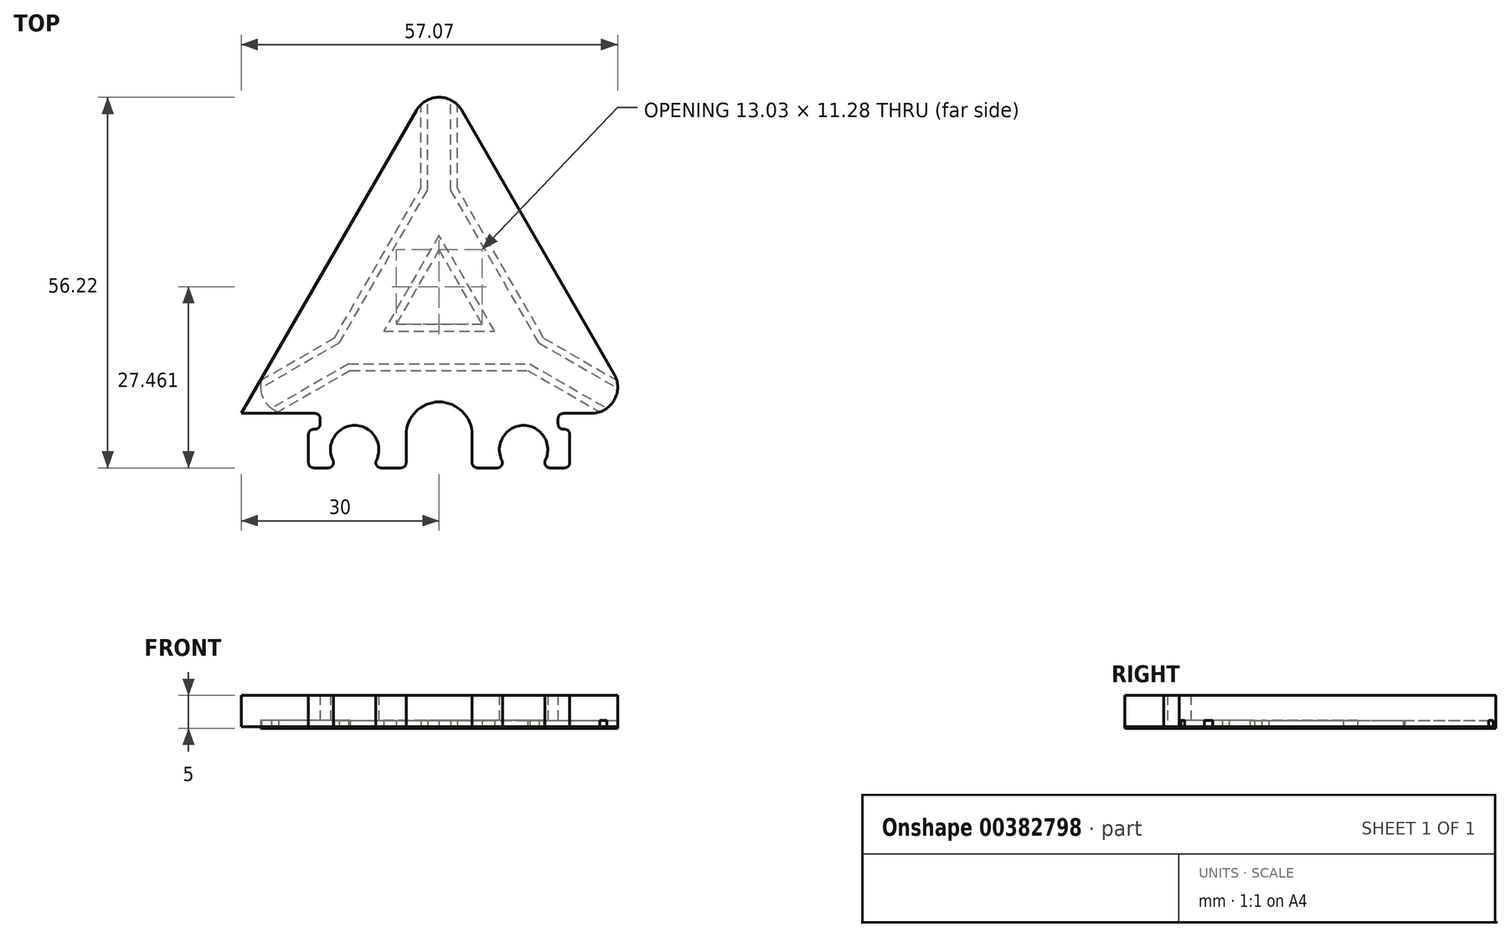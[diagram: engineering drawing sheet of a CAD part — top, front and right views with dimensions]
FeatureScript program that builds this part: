
annotation { "Feature Type Name" : "Feature", "Feature Type Description" : "" }
export const myFeature = defineFeature(function(context is Context, id is Id, definition is map)
    precondition{}
    {
        {
            var Q0;
            Q0=qCreatedBy(makeId("Top.planeOp"),FACE);
            var sketch = newSketch(context, id + "F0", { "sketchPlane" : qUnion([Q0])});
            skArc(sketch, "E0", {"start": v(0, 5) * mm, "mid": v(-3.54, 3.54) * mm, "end": v(-5, 0) * mm});
            skLineSegment(sketch, "E1", {"start": v(-5, 0) * mm, "end": v(-5, -5) * mm});
            skPoint(sketch, "E2.start.orphan", {"position": v(0, 5) * mm});
            skPoint(sketch, "E3.start.orphan", {"position": v(0, -5) * mm});
            skLineSegment(sketch, "E4", {"start": v(-5, -5) * mm, "end": v(-10.4, -5) * mm});
            skArc(sketch, "E5", {"start": v(-10.4, -5) * mm, "mid": v(-12.8, 1.43) * mm, "end": v(-15.22, -5) * mm});
            skPoint(sketch, "E6.end.orphan", {"position": v(-15.22, -5) * mm});
            skPoint(sketch, "E7.start.orphan", {"position": v(-12.8, -5) * mm});
            skLineSegment(sketch, "E8", {"start": v(-15.22, -5) * mm, "end": v(-19.82, -5) * mm});
            skLineSegment(sketch, "E9", {"start": v(-19.82, -5) * mm, "end": v(-19.82, 0.86) * mm});
            skLineSegment(sketch, "E10", {"start": v(-19.82, 0.86) * mm, "end": v(-18.04, 0.86) * mm});
            skLineSegment(sketch, "E11", {"start": v(-18.04, 0.86) * mm, "end": v(-18.04, 3.26) * mm});
            skLineSegment(sketch, "E12", {"start": v(0, -5) * mm, "end": v(0, -3.9) * mm});
            skLineSegment(sketch, "E13", {"start": v(0, 10.27) * mm, "end": v(0, -5) * mm, "construction": true});
            skArc(sketch, "E14.MirrorCS", {"start": v(0, 5) * mm, "mid": v(3.54, 3.54) * mm, "end": v(5, 0) * mm});
            skLineSegment(sketch, "E15.MirrorCS", {"start": v(5, 0) * mm, "end": v(5, -5) * mm});
            skLineSegment(sketch, "E16.MirrorCS", {"start": v(5, -5) * mm, "end": v(10.4, -5) * mm});
            skArc(sketch, "E17.MirrorCS", {"start": v(10.4, -5) * mm, "mid": v(12.8, 1.43) * mm, "end": v(15.22, -5) * mm});
            skLineSegment(sketch, "E18.MirrorCS", {"start": v(15.22, -5) * mm, "end": v(19.82, -5) * mm});
            skLineSegment(sketch, "E19.MirrorCS", {"start": v(19.82, -5) * mm, "end": v(19.82, 0.86) * mm});
            skLineSegment(sketch, "E20.MirrorCS", {"start": v(19.82, 0.86) * mm, "end": v(18.04, 0.86) * mm});
            skLineSegment(sketch, "E21.MirrorCS", {"start": v(18.04, 0.86) * mm, "end": v(18.04, 3.26) * mm});
            skLineSegment(sketch, "E22", {"start": v(-18.04, 3.26) * mm, "end": v(-30, 3.26) * mm});
            skLineSegment(sketch, "E23.bottom", {"start": v(-30, 3.26) * mm, "end": v(-18.04, 3.26) * mm});
            skLineSegment(sketch, "E24.trimOffspring", {"start": v(18.04, 3.26) * mm, "end": v(30, 3.26) * mm});
            skLineSegment(sketch, "E25", {"start": v(-30, 3.26) * mm, "end": v(0, 55.22) * mm});
            skLineSegment(sketch, "E26", {"start": v(30, 3.26) * mm, "end": v(0, 55.22) * mm});
            skSolve(sketch);
        }
        {
            var Q0;
            Q0=makeQuery(id+"F0.imprint","IMPRINT",FACE,{"disambiguationData":[TD([[makeQuery(id+"F0.imprint","IMPRINT",EDGE,{"derivedFrom":sQuery(id+"F0.wireOp",EDGE,"E0")}),-1.0]])]});
            extrude(context, id + "F1", {"entities" : qUnion([Q0]), "depth" : 4.8 * mm});
        }
        {
            var Q0;
            Q0=makeQuery(id+"F1.opExtrude","SWEPT_EDGE",EDGE,{"disambiguationData":[OSD([sQuery(id+"F0.wireOp",EDGE,"E24.trimOffspring"),sQuery(id+"F0.wireOp",EDGE,"E26")])]});
            var Q1;
            Q1=makeQuery(id+"F1.opExtrude","SWEPT_EDGE",EDGE,{"disambiguationData":[OSD([sQuery(id+"F0.wireOp",EDGE,"E25"),sQuery(id+"F0.wireOp",EDGE,"E26")])]});
            var Q2;
            Q2=makeQuery(id+"F1.opExtrude","SWEPT_EDGE",EDGE,{"disambiguationData":[OSD([sQuery(id+"F0.wireOp",EDGE,"E23.bottom"),sQuery(id+"F0.wireOp",EDGE,"E25")])]});
            fillet(context, id + "F2", {"entities" : qUnion([Q0, Q1, Q2]), "radius" : 4 * mm, "tangentPropagation" : true, "allowEdgeOverflow" : false});
        }
        {
            var Q0;
            Q0=makeQuery(id+"F1.opExtrude","CAP_FACE",FACE,{"disambiguationData":[OSD([sQuery(id+"F0.wireOp",EDGE,"E0"),sQuery(id+"F0.wireOp",EDGE,"E1"),sQuery(id+"F0.wireOp",EDGE,"E4"),sQuery(id+"F0.wireOp",EDGE,"E5"),sQuery(id+"F0.wireOp",EDGE,"E8"),sQuery(id+"F0.wireOp",EDGE,"E9"),sQuery(id+"F0.wireOp",EDGE,"E10"),sQuery(id+"F0.wireOp",EDGE,"E11"),sQuery(id+"F0.wireOp",EDGE,"E14.MirrorCS"),sQuery(id+"F0.wireOp",EDGE,"E15.MirrorCS"),sQuery(id+"F0.wireOp",EDGE,"E16.MirrorCS"),sQuery(id+"F0.wireOp",EDGE,"E17.MirrorCS"),sQuery(id+"F0.wireOp",EDGE,"E18.MirrorCS"),sQuery(id+"F0.wireOp",EDGE,"E19.MirrorCS"),sQuery(id+"F0.wireOp",EDGE,"E20.MirrorCS"),sQuery(id+"F0.wireOp",EDGE,"E21.MirrorCS"),sQuery(id+"F0.wireOp",EDGE,"E23.bottom"),sQuery(id+"F0.wireOp",EDGE,"E24.trimOffspring"),sQuery(id+"F0.wireOp",EDGE,"E25"),sQuery(id+"F0.wireOp",EDGE,"E26")])],"isStart":true});
            var sketch = newSketch(context, id + "F3", { "sketchPlane" : qUnion([Q0])});
            skPoint(sketch, "E27.orphan", {"position": v(15, -29.24) * mm});
            skPoint(sketch, "E28", {"position": v(0, -20.58) * mm});
            skPoint(sketch, "E29.start.orphan", {"position": v(0, -51.22) * mm});
            skPoint(sketch, "E30.end.orphan", {"position": v(-26.54, -5.26) * mm});
            skArc(sketch, "E31.cCircle", {"start": v(-8.49, -25.48) * mm, "mid": v(8.49, -25.48) * mm, "end": v(0, -10.78) * mm, "construction": true});
            skLineSegment(sketch, "E31.0", {"start": v(0, -10.78) * mm, "end": v(13.74, -10.78) * mm});
            skLineSegment(sketch, "E31.1", {"start": v(15.15, -13.95) * mm, "end": v(1.74, -37.18) * mm});
            skPoint(sketch, "E31.0.midPoint", {"position": v(0, -10.78) * mm});
            skLineSegment(sketch, "E32.MirrorCS", {"start": v(13.74, -10.78) * mm, "end": v(0, -10.78) * mm});
            skPoint(sketch, "E33.start.orphan", {"position": v(8.49, -25.48) * mm});
            skPoint(sketch, "E34.orphan", {"position": v(-16.98, -10.78) * mm});
            skLineSegment(sketch, "E35", {"start": v(15.15, -13.95) * mm, "end": v(27.07, -7.07) * mm});
            skLineSegment(sketch, "E36", {"start": v(13.74, -10.78) * mm, "end": v(25.43, -4.03) * mm});
            skPoint(sketch, "E37.orphan", {"position": v(16.98, -10.78) * mm});
            skLineSegment(sketch, "E38.MirrorCS", {"start": v(1.74, -37.18) * mm, "end": v(1.74, -50.82) * mm});
            skPoint(sketch, "E39.orphan", {"position": v(0, -40.19) * mm});
            skCircle(sketch, "E40.cCircle", {"center": v(0, -20.58) * mm, "radius": 3.76 * mm, "construction": true});
            skPoint(sketch, "E40.0.midPoint", {"position": v(0, -16.82) * mm});
            skPoint(sketch, "E41.orphan", {"position": v(0, -28.1) * mm});
            skPoint(sketch, "E42.orphan", {"position": v(-6.51, -16.82) * mm});
            skPoint(sketch, "E40.1.start.orphan", {"position": v(6.51, -16.82) * mm});
            skLineSegment(sketch, "E43.0", {"start": v(2.74, -37.45) * mm, "end": v(2.74, -50.14) * mm});
            skLineSegment(sketch, "E43.1", {"start": v(15.88, -14.68) * mm, "end": v(2.74, -37.45) * mm});
            skLineSegment(sketch, "E43.2", {"start": v(15.88, -14.68) * mm, "end": v(26.93, -8.3) * mm});
            skLineSegment(sketch, "E44.1", {"start": v(13.47, -9.78) * mm, "end": v(0, -9.78) * mm});
            skLineSegment(sketch, "E44.2", {"start": v(13.47, -9.78) * mm, "end": v(24.38, -3.48) * mm});
            skLineSegment(sketch, "E45.0", {"start": v(-6.51, -16.82) * mm, "end": v(6.51, -16.82) * mm});
            skLineSegment(sketch, "E45.1", {"start": v(6.51, -16.82) * mm, "end": v(0, -28.1) * mm});
            skLineSegment(sketch, "E45.2", {"start": v(0, -28.1) * mm, "end": v(-6.51, -16.82) * mm});
            skCircle(sketch, "E46.cCircle", {"center": v(0, -20.58) * mm, "radius": 4.86 * mm, "construction": true});
            skLineSegment(sketch, "E46.0", {"start": v(-8.42, -15.72) * mm, "end": v(8.42, -15.72) * mm});
            skLineSegment(sketch, "E46.1", {"start": v(8.42, -15.72) * mm, "end": v(0, -30.3) * mm});
            skLineSegment(sketch, "E46.2", {"start": v(0, -30.3) * mm, "end": v(-8.42, -15.72) * mm});
            skPoint(sketch, "E46.0.midPoint", {"position": v(0, -15.72) * mm});
            skArc(sketch, "E47.0", {"start": v(26.93, -8.3) * mm, "mid": v(27.05, -7.7) * mm, "end": v(27.07, -7.07) * mm});
            skPoint(sketch, "E48.orphan", {"position": v(-26.54, -9.26) * mm});
            skPoint(sketch, "E49.orphan", {"position": v(-23.07, -3.26) * mm});
            skArc(sketch, "E50.trimOffspring", {"start": v(-26.54, -5.26) * mm, "mid": v(-27.02, -6.63) * mm, "end": v(-26.99, -8.08) * mm});
            skPoint(sketch, "E51.orphan", {"position": v(26.76, -3.26) * mm});
            skArc(sketch, "E52.trimOffspring", {"start": v(25.43, -4.03) * mm, "mid": v(24.92, -3.71) * mm, "end": v(24.38, -3.48) * mm});
            skPoint(sketch, "E53.orphan", {"position": v(26.54, -9.26) * mm});
            skPoint(sketch, "E54.orphan", {"position": v(23.07, -3.26) * mm});
            skArc(sketch, "E55.trimOffspring", {"start": v(0, -51.22) * mm, "mid": v(2, -50.69) * mm, "end": v(3.46, -49.22) * mm});
            skLineSegment(sketch, "E56", {"start": v(0, -5) * mm, "end": v(0, -56.8) * mm});
            skPoint(sketch, "E57.0.start.orphan", {"position": v(-3.46, -49.22) * mm});
            skLineSegment(sketch, "E58.MirrorCS", {"start": v(-15.15, -13.95) * mm, "end": v(-1.74, -37.18) * mm});
            skLineSegment(sketch, "E59.MirrorCS", {"start": v(-15.88, -14.68) * mm, "end": v(-2.74, -37.45) * mm});
            skLineSegment(sketch, "E60.MirrorCS", {"start": v(-2.74, -37.45) * mm, "end": v(-2.74, -50.14) * mm});
            skLineSegment(sketch, "E61.MirrorCS", {"start": v(-1.74, -37.18) * mm, "end": v(-1.74, -50.82) * mm});
            skLineSegment(sketch, "E62.MirrorCS", {"start": v(-15.88, -14.68) * mm, "end": v(-26.93, -8.3) * mm});
            skLineSegment(sketch, "E63.MirrorCS", {"start": v(-15.15, -13.95) * mm, "end": v(-27.07, -7.07) * mm});
            skLineSegment(sketch, "E64.MirrorCS", {"start": v(-13.74, -10.78) * mm, "end": v(0, -10.78) * mm});
            skLineSegment(sketch, "E65.MirrorCS", {"start": v(-13.47, -9.78) * mm, "end": v(0, -9.78) * mm});
            skLineSegment(sketch, "E66.MirrorCS", {"start": v(-13.47, -9.78) * mm, "end": v(-24.38, -3.48) * mm});
            skLineSegment(sketch, "E67.MirrorCS", {"start": v(-13.74, -10.78) * mm, "end": v(-25.43, -4.03) * mm});
            skArc(sketch, "E68.0", {"start": v(-2.74, -50.14) * mm, "mid": v(-2.26, -50.52) * mm, "end": v(-1.74, -50.82) * mm});
            skArc(sketch, "E69.0", {"start": v(-24.38, -3.48) * mm, "mid": v(-24.92, -3.71) * mm, "end": v(-25.43, -4.03) * mm});
            skArc(sketch, "E70.trimOffspring", {"start": v(-27.07, -7.07) * mm, "mid": v(-27.05, -7.7) * mm, "end": v(-26.93, -8.3) * mm});
            skArc(sketch, "E71.trimOffspring", {"start": v(1.74, -50.82) * mm, "mid": v(2.26, -50.52) * mm, "end": v(2.74, -50.14) * mm});
            skSolve(sketch);
        }
        {
            var Q0;
            Q0 = qSketchRegion(id + "F3", true);
            extrude(context, id + "F4", {"entities" : qUnion([Q0]), "operationType" : NewBodyOperationType.REMOVE, "oppositeDirection" : true, "depth" : 1 * mm});
        }
        {
            var Q0;
            Q0 = qSketchRegion(id + "F3", true);
            extrude(context, id + "F5", {"entities" : qUnion([Q0]), "oppositeDirection" : true, "depth" : 1 * mm});
        }
        {
            var Q0;
            Q0=makeQuery(id+"F1.opExtrude","SWEPT_EDGE",EDGE,{"disambiguationData":[OSD([sQuery(id+"F0.wireOp",EDGE,"E21.MirrorCS"),sQuery(id+"F0.wireOp",EDGE,"E24.trimOffspring")])]});
            var Q1;
            Q1=makeQuery(id+"F1.opExtrude","SWEPT_EDGE",EDGE,{"disambiguationData":[OSD([sQuery(id+"F0.wireOp",EDGE,"E20.MirrorCS"),sQuery(id+"F0.wireOp",EDGE,"E21.MirrorCS")])]});
            var Q2;
            Q2=makeQuery(id+"F1.opExtrude","SWEPT_EDGE",EDGE,{"disambiguationData":[OSD([sQuery(id+"F0.wireOp",EDGE,"E19.MirrorCS"),sQuery(id+"F0.wireOp",EDGE,"E20.MirrorCS")])]});
            var Q3;
            Q3=makeQuery(id+"F1.opExtrude","SWEPT_EDGE",EDGE,{"disambiguationData":[OSD([sQuery(id+"F0.wireOp",EDGE,"E18.MirrorCS"),sQuery(id+"F0.wireOp",EDGE,"E19.MirrorCS")])]});
            var Q4;
            Q4=makeQuery(id+"F1.opExtrude","SWEPT_EDGE",EDGE,{"disambiguationData":[OSD([sQuery(id+"F0.wireOp",EDGE,"E17.MirrorCS"),sQuery(id+"F0.wireOp",EDGE,"E18.MirrorCS")])]});
            var Q5;
            Q5=makeQuery(id+"F1.opExtrude","SWEPT_EDGE",EDGE,{"disambiguationData":[OSD([sQuery(id+"F0.wireOp",EDGE,"E16.MirrorCS"),sQuery(id+"F0.wireOp",EDGE,"E17.MirrorCS")])]});
            var Q6;
            Q6=makeQuery(id+"F1.opExtrude","SWEPT_EDGE",EDGE,{"disambiguationData":[OSD([sQuery(id+"F0.wireOp",EDGE,"E15.MirrorCS"),sQuery(id+"F0.wireOp",EDGE,"E16.MirrorCS")])]});
            var Q7;
            Q7=makeQuery(id+"F1.opExtrude","SWEPT_EDGE",EDGE,{"disambiguationData":[OSD([sQuery(id+"F0.wireOp",EDGE,"E1"),sQuery(id+"F0.wireOp",EDGE,"E4")])]});
            var Q8;
            Q8=makeQuery(id+"F1.opExtrude","SWEPT_EDGE",EDGE,{"disambiguationData":[OSD([sQuery(id+"F0.wireOp",EDGE,"E4"),sQuery(id+"F0.wireOp",EDGE,"E5")])]});
            var Q9;
            Q9=makeQuery(id+"F1.opExtrude","SWEPT_EDGE",EDGE,{"disambiguationData":[OSD([sQuery(id+"F0.wireOp",EDGE,"E5"),sQuery(id+"F0.wireOp",EDGE,"E8")])]});
            var Q10;
            Q10=makeQuery(id+"F1.opExtrude","SWEPT_EDGE",EDGE,{"disambiguationData":[OSD([sQuery(id+"F0.wireOp",EDGE,"E8"),sQuery(id+"F0.wireOp",EDGE,"E9")])]});
            var Q11;
            Q11=makeQuery(id+"F1.opExtrude","SWEPT_EDGE",EDGE,{"disambiguationData":[OSD([sQuery(id+"F0.wireOp",EDGE,"E9"),sQuery(id+"F0.wireOp",EDGE,"E10")])]});
            var Q12;
            Q12=makeQuery(id+"F1.opExtrude","SWEPT_EDGE",EDGE,{"disambiguationData":[OSD([sQuery(id+"F0.wireOp",EDGE,"E10"),sQuery(id+"F0.wireOp",EDGE,"E11")])]});
            var Q13;
            Q13=makeQuery(id+"F1.opExtrude","SWEPT_EDGE",EDGE,{"disambiguationData":[OSD([sQuery(id+"F0.wireOp",EDGE,"E11"),sQuery(id+"F0.wireOp",EDGE,"E23.bottom")])]});
            fillet(context, id + "F6", {"entities" : qUnion([Q0, Q1, Q2, Q3, Q4, Q5, Q6, Q7, Q8, Q9, Q10, Q11, Q12, Q13]), "radius" : .8 * mm, "tangentPropagation" : true, "allowEdgeOverflow" : false});
        }
        {
            var Q0;
            {var subQ0=sQuery(id+"F0.wireOp",EDGE,"E26");var subQ1=sQuery(id+"F0.wireOp",EDGE,"E25");var subQ2=sQuery(id+"F0.wireOp",EDGE,"E24.trimOffspring");Q0=makeQuery(id+"F4.boolean.opBoolean","SPLIT",FACE,{"disambiguationData":[TD([makeQuery(id+"F1.opExtrude","SWEPT_FACE",FACE,{"disambiguationData":[OSD([subQ0])]})])],"derivedFrom":makeQuery(id+"F1.opExtrude","CAP_FACE",FACE,{"disambiguationData":[OSD([sQuery(id+"F0.wireOp",EDGE,"E0"),sQuery(id+"F0.wireOp",EDGE,"E1"),sQuery(id+"F0.wireOp",EDGE,"E4"),sQuery(id+"F0.wireOp",EDGE,"E5"),sQuery(id+"F0.wireOp",EDGE,"E8"),sQuery(id+"F0.wireOp",EDGE,"E9"),sQuery(id+"F0.wireOp",EDGE,"E10"),sQuery(id+"F0.wireOp",EDGE,"E11"),sQuery(id+"F0.wireOp",EDGE,"E14.MirrorCS"),sQuery(id+"F0.wireOp",EDGE,"E15.MirrorCS"),sQuery(id+"F0.wireOp",EDGE,"E16.MirrorCS"),sQuery(id+"F0.wireOp",EDGE,"E17.MirrorCS"),sQuery(id+"F0.wireOp",EDGE,"E18.MirrorCS"),sQuery(id+"F0.wireOp",EDGE,"E19.MirrorCS"),sQuery(id+"F0.wireOp",EDGE,"E20.MirrorCS"),sQuery(id+"F0.wireOp",EDGE,"E21.MirrorCS"),sQuery(id+"F0.wireOp",EDGE,"E23.bottom"),subQ2,subQ1,subQ0])],"isStart":true})});}
            var sketch = newSketch(context, id + "F7", { "sketchPlane" : qUnion([Q0])});
            skLineSegment(sketch, "E72.0", {"start": v(26.54, -9.26) * mm, "end": v(3.46, -49.22) * mm});
            skArc(sketch, "E73.0", {"start": v(2.74, -50.14) * mm, "mid": v(3.13, -49.7) * mm, "end": v(3.46, -49.22) * mm});
            skPoint(sketch, "E74.0", {"position": v(2.26, -50.52) * mm});
            skArc(sketch, "E75.0", {"start": v(1.74, -50.82) * mm, "mid": v(2.26, -50.52) * mm, "end": v(2.74, -50.14) * mm});
            skArc(sketch, "E76.0", {"start": v(-1.74, -50.82) * mm, "mid": v(0, -51.22) * mm, "end": v(1.74, -50.82) * mm});
            skArc(sketch, "E77.0", {"start": v(-2.74, -50.14) * mm, "mid": v(-2.26, -50.52) * mm, "end": v(-1.74, -50.82) * mm});
            skArc(sketch, "E78.0", {"start": v(-3.46, -49.22) * mm, "mid": v(-3.13, -49.7) * mm, "end": v(-2.74, -50.14) * mm});
            skLineSegment(sketch, "E79.0", {"start": v(-26.54, -9.26) * mm, "end": v(-3.46, -49.22) * mm});
            skArc(sketch, "E80.0", {"start": v(-26.93, -8.3) * mm, "mid": v(-26.77, -8.8) * mm, "end": v(-26.54, -9.26) * mm});
            skArc(sketch, "E80.1", {"start": v(-27.07, -7.07) * mm, "mid": v(-27.05, -7.7) * mm, "end": v(-26.93, -8.3) * mm});
            skArc(sketch, "E80.2", {"start": v(-25.43, -4.03) * mm, "mid": v(-26.6, -5.36) * mm, "end": v(-27.07, -7.07) * mm});
            skArc(sketch, "E81.0", {"start": v(-24.38, -3.48) * mm, "mid": v(-24.92, -3.71) * mm, "end": v(-25.43, -4.03) * mm});
            skArc(sketch, "E82.0", {"start": v(-23.07, -3.26) * mm, "mid": v(-23.73, -3.32) * mm, "end": v(-24.38, -3.48) * mm});
            skLineSegment(sketch, "E83.0", {"start": v(-23.07, -3.26) * mm, "end": v(-18.84, -3.26) * mm});
            skArc(sketch, "E84.0", {"start": v(-18.04, -2.46) * mm, "mid": v(-18.27, -3.03) * mm, "end": v(-18.84, -3.26) * mm});
            skLineSegment(sketch, "E85.0", {"start": v(-18.04, -1.66) * mm, "end": v(-18.04, -2.46) * mm});
            skArc(sketch, "E86.0", {"start": v(-18.84, -0.86) * mm, "mid": v(-18.27, -1.1) * mm, "end": v(-18.04, -1.66) * mm});
            skArc(sketch, "E87.0", {"start": v(-19.82, -0.06) * mm, "mid": v(-19.58, -0.63) * mm, "end": v(-19.02, -0.86) * mm});
            skPoint(sketch, "E88.0", {"position": v(-18.93, -0.86) * mm});
            skLineSegment(sketch, "E89.0", {"start": v(-19.02, -0.86) * mm, "end": v(-18.84, -0.86) * mm});
            skLineSegment(sketch, "E90.0", {"start": v(-19.82, 4.2) * mm, "end": v(-19.82, -0.06) * mm});
            skArc(sketch, "E91.0", {"start": v(-19.02, 5) * mm, "mid": v(-19.58, 4.77) * mm, "end": v(-19.82, 4.2) * mm});
            skLineSegment(sketch, "E92.0", {"start": v(-16.82, 5) * mm, "end": v(-19.02, 5) * mm});
            skArc(sketch, "E93.0", {"start": v(-16.1, 3.85) * mm, "mid": v(-16.14, 4.62) * mm, "end": v(-16.82, 5) * mm});
            skArc(sketch, "E94.0", {"start": v(-9.52, 3.85) * mm, "mid": v(-12.8, -1.43) * mm, "end": v(-16.1, 3.85) * mm});
            skArc(sketch, "E95.0", {"start": v(-8.8, 5) * mm, "mid": v(-9.48, 4.62) * mm, "end": v(-9.52, 3.85) * mm});
            skLineSegment(sketch, "E96.0", {"start": v(-5.8, 5) * mm, "end": v(-8.8, 5) * mm});
            skArc(sketch, "E97.0", {"start": v(-5, 4.2) * mm, "mid": v(-5.23, 4.77) * mm, "end": v(-5.8, 5) * mm});
            skLineSegment(sketch, "E98.0", {"start": v(-5, 0) * mm, "end": v(-5, 4.2) * mm});
            skArc(sketch, "E99.0", {"start": v(5, 0) * mm, "mid": v(0, -5) * mm, "end": v(-5, 0) * mm});
            skLineSegment(sketch, "E100.0", {"start": v(5, 0) * mm, "end": v(5, 4.2) * mm});
            skPoint(sketch, "E101.0", {"position": v(5.23, 4.77) * mm});
            skLineSegment(sketch, "E102.0", {"start": v(5.8, 5) * mm, "end": v(8.8, 5) * mm});
            skArc(sketch, "E103.0", {"start": v(9.52, 3.85) * mm, "mid": v(12.8, -1.43) * mm, "end": v(16.1, 3.85) * mm});
            skPoint(sketch, "E104.0", {"position": v(9.48, 4.62) * mm});
            skArc(sketch, "E105.0", {"start": v(9.52, 3.85) * mm, "mid": v(9.48, 4.62) * mm, "end": v(8.8, 5) * mm});
            skArc(sketch, "E106.0", {"start": v(16.82, 5) * mm, "mid": v(16.14, 4.62) * mm, "end": v(16.1, 3.85) * mm});
            skLineSegment(sketch, "E107.0", {"start": v(16.82, 5) * mm, "end": v(19.02, 5) * mm});
            skLineSegment(sketch, "E108.0", {"start": v(19.82, 4.2) * mm, "end": v(19.82, -0.06) * mm});
            skArc(sketch, "E109.0", {"start": v(19.02, -0.86) * mm, "mid": v(19.58, -0.63) * mm, "end": v(19.82, -0.06) * mm});
            skArc(sketch, "E110.0", {"start": v(19.82, 4.2) * mm, "mid": v(19.58, 4.77) * mm, "end": v(19.02, 5) * mm});
            skArc(sketch, "E111.0", {"start": v(18.04, -1.66) * mm, "mid": v(18.27, -1.1) * mm, "end": v(18.84, -0.86) * mm});
            skPoint(sketch, "E112.0", {"position": v(18.93, -0.86) * mm});
            skLineSegment(sketch, "E113.0", {"start": v(19.02, -0.86) * mm, "end": v(18.84, -0.86) * mm});
            skPoint(sketch, "E114.0", {"position": v(18.04, -2.06) * mm});
            skLineSegment(sketch, "E115.0", {"start": v(18.04, -1.66) * mm, "end": v(18.04, -2.46) * mm});
            skArc(sketch, "E116.0", {"start": v(18.84, -3.26) * mm, "mid": v(18.27, -3.03) * mm, "end": v(18.04, -2.46) * mm});
            skLineSegment(sketch, "E117.0.6", {"start": v(-18.84, -3.26) * mm, "end": v(-23.07, -3.26) * mm});
            skLineSegment(sketch, "E117.0.8", {"start": v(-24.38, -3.48) * mm, "end": v(-13.47, -9.78) * mm});
            skLineSegment(sketch, "E117.0.9", {"start": v(-13.47, -9.78) * mm, "end": v(13.47, -9.78) * mm});
            skLineSegment(sketch, "E117.0.10", {"start": v(13.47, -9.78) * mm, "end": v(24.38, -3.48) * mm});
            skArc(sketch, "E117.0.11", {"start": v(24.38, -3.48) * mm, "mid": v(23.73, -3.32) * mm, "end": v(23.07, -3.26) * mm});
            skLineSegment(sketch, "E117.0.12", {"start": v(23.07, -3.26) * mm, "end": v(18.84, -3.26) * mm});
            skLineSegment(sketch, "E117.0.14", {"start": v(18.04, -2.46) * mm, "end": v(18.04, -1.66) * mm});
            skLineSegment(sketch, "E117.0.16", {"start": v(18.84, -0.86) * mm, "end": v(19.02, -0.86) * mm});
            skLineSegment(sketch, "E117.0.18", {"start": v(19.82, -0.06) * mm, "end": v(19.82, 4.2) * mm});
            skLineSegment(sketch, "E117.0.20", {"start": v(19.02, 5) * mm, "end": v(16.82, 5) * mm});
            skArc(sketch, "E117.0.22", {"start": v(16.1, 3.85) * mm, "mid": v(12.8, -1.43) * mm, "end": v(9.52, 3.85) * mm});
            skLineSegment(sketch, "E117.0.24", {"start": v(8.8, 5) * mm, "end": v(5.8, 5) * mm});
            skArc(sketch, "E117.0.25", {"start": v(5.8, 5) * mm, "mid": v(5.23, 4.77) * mm, "end": v(5, 4.2) * mm});
            skLineSegment(sketch, "E117.0.26", {"start": v(5, 4.2) * mm, "end": v(5, 0) * mm});
            skPoint(sketch, "E118.0", {"position": v(20.95, -3.26) * mm});
            skArc(sketch, "E119.0", {"start": v(25.43, -4.03) * mm, "mid": v(24.92, -3.71) * mm, "end": v(24.38, -3.48) * mm});
            skArc(sketch, "E120.0", {"start": v(27.07, -7.07) * mm, "mid": v(26.6, -5.36) * mm, "end": v(25.43, -4.03) * mm});
            skArc(sketch, "E121.0", {"start": v(26.93, -8.3) * mm, "mid": v(27.05, -7.7) * mm, "end": v(27.07, -7.07) * mm});
            skArc(sketch, "E122.0", {"start": v(26.54, -9.26) * mm, "mid": v(26.77, -8.8) * mm, "end": v(26.93, -8.3) * mm});
            skSolve(sketch);
        }
        {
            var Q0;
            Q0 = qSketchRegion(id + "F7", true);
            extrude(context, id + "F8", {"entities" : qUnion([Q0]), "depth" : .2 * mm});
        }
    });
